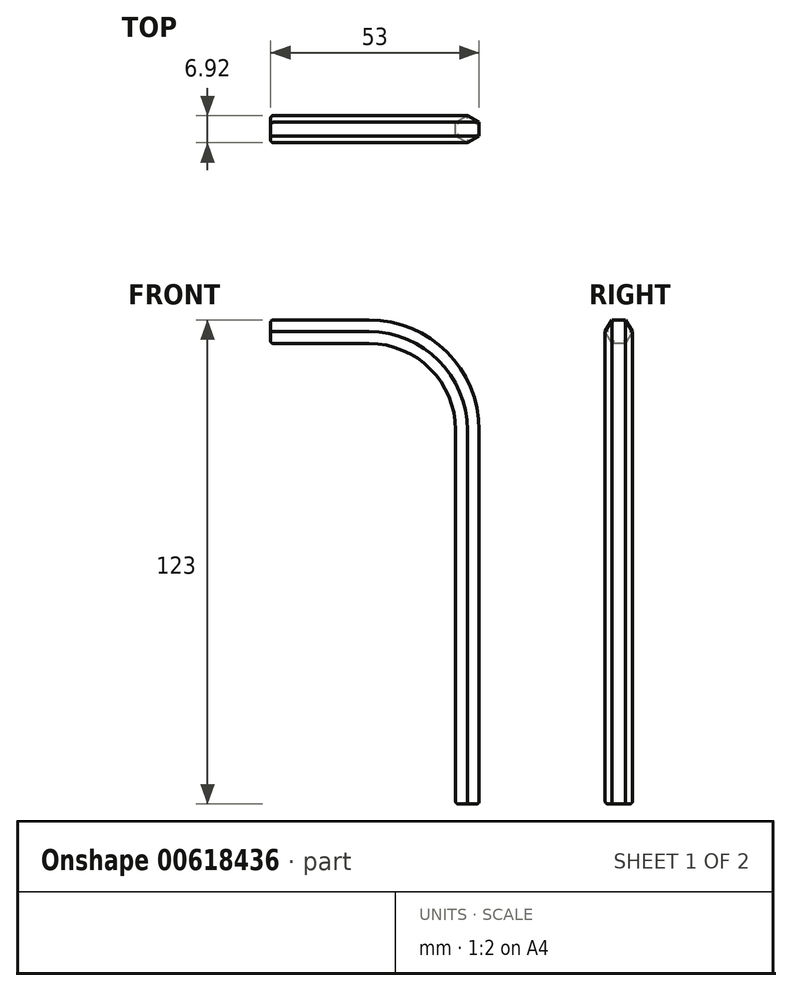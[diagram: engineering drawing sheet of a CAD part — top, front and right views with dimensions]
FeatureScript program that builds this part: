
annotation { "Feature Type Name" : "Feature", "Feature Type Description" : "" }
export const myFeature = defineFeature(function(context is Context, id is Id, definition is map)
    precondition{}
    {
        {
            var Q0;
            Q0=qCreatedBy(makeId("Front.planeOp"),FACE);
            var sketch = newSketch(context, id + "F0", { "sketchPlane" : qUnion([Q0])});
            skLineSegment(sketch, "E0", {"start": v(0, 0) * mm, "end": v(25, 0) * mm});
            skLineSegment(sketch, "E1", {"start": v(50, -25) * mm, "end": v(50, -120) * mm});
            skPoint(sketch, "E2.visualSharp", {"position": v(50, 0) * mm});
            skArc(sketch, "E2.filletArc", {"start": v(50, -25) * mm, "mid": v(42.68, -7.32) * mm, "end": v(25, 0) * mm});
            skSolve(sketch);
        }
        {
            var Q0;
            Q0=qCreatedBy(makeId("Right.planeOp"),FACE);
            var sketch = newSketch(context, id + "F1", { "sketchPlane" : qUnion([Q0])});
            skCircle(sketch, "E3.cCircle", {"center": v(0, 0) * mm, "radius": 3 * mm, "construction": true});
            skLineSegment(sketch, "E3.0", {"start": v(-3.46, 0) * mm, "end": v(-1.73, 3) * mm});
            skLineSegment(sketch, "E3.1", {"start": v(-1.73, 3) * mm, "end": v(1.73, 3) * mm});
            skLineSegment(sketch, "E3.2", {"start": v(1.73, 3) * mm, "end": v(3.46, 0) * mm});
            skLineSegment(sketch, "E3.3", {"start": v(3.46, 0) * mm, "end": v(1.73, -3) * mm});
            skLineSegment(sketch, "E3.4", {"start": v(1.73, -3) * mm, "end": v(-1.73, -3) * mm});
            skLineSegment(sketch, "E3.5", {"start": v(-1.73, -3) * mm, "end": v(-3.46, 0) * mm});
            skPoint(sketch, "E3.0.midPoint", {"position": v(-2.6, 1.5) * mm});
            skSolve(sketch);
        }
        {
            var Q0;
            Q0=makeQuery(id+"F1.imprint","IMPRINT",FACE,{"disambiguationData":[TD([[makeQuery(id+"F1.imprint","IMPRINT",EDGE,{"derivedFrom":sQuery(id+"F1.wireOp",EDGE,"E3.0")}),-1.0]])]});
            var Q1;
            Q1=sQuery(id+"F0.wireOp",EDGE,"E0");
            var Q2;
            Q2=sQuery(id+"F0.wireOp",EDGE,"E2.filletArc");
            var Q3;
            Q3=sQuery(id+"F0.wireOp",EDGE,"E1");
            sweep(context, id + "F2", {"profiles" : qUnion([Q0]), "path" : qUnion([Q1, Q2, Q3])});
        }
        {
            var Q0;
            Q0=makeQuery(id+"F2.opSweep","CAP_FACE",FACE,{"disambiguationData":[OSD([sQuery(id+"F0.wireOp",VERTEX,"E0.start"),sQuery(id+"F1.wireOp",EDGE,"E3.0"),sQuery(id+"F1.wireOp",EDGE,"E3.1"),sQuery(id+"F1.wireOp",EDGE,"E3.2"),sQuery(id+"F1.wireOp",EDGE,"E3.3"),sQuery(id+"F1.wireOp",EDGE,"E3.4"),sQuery(id+"F1.wireOp",EDGE,"E3.5")])],"isStart":true});
            fillet(context, id + "F3", {"entities" : qUnion([Q0]), "radius" : .7 * mm, "tangentPropagation" : true, "allowEdgeOverflow" : false});
        }
        {
            var Q0;
            Q0=makeQuery(id+"F2.opSweep","CAP_FACE",FACE,{"disambiguationData":[OSD([sQuery(id+"F0.wireOp",VERTEX,"E1.end"),sQuery(id+"F1.wireOp",EDGE,"E3.0"),sQuery(id+"F1.wireOp",EDGE,"E3.1"),sQuery(id+"F1.wireOp",EDGE,"E3.2"),sQuery(id+"F1.wireOp",EDGE,"E3.3"),sQuery(id+"F1.wireOp",EDGE,"E3.4"),sQuery(id+"F1.wireOp",EDGE,"E3.5")])],"isStart":false});
            fillet(context, id + "F4", {"entities" : qUnion([Q0]), "radius" : 0.7 * mm, "tangentPropagation" : true, "allowEdgeOverflow" : false});
        }
    });
